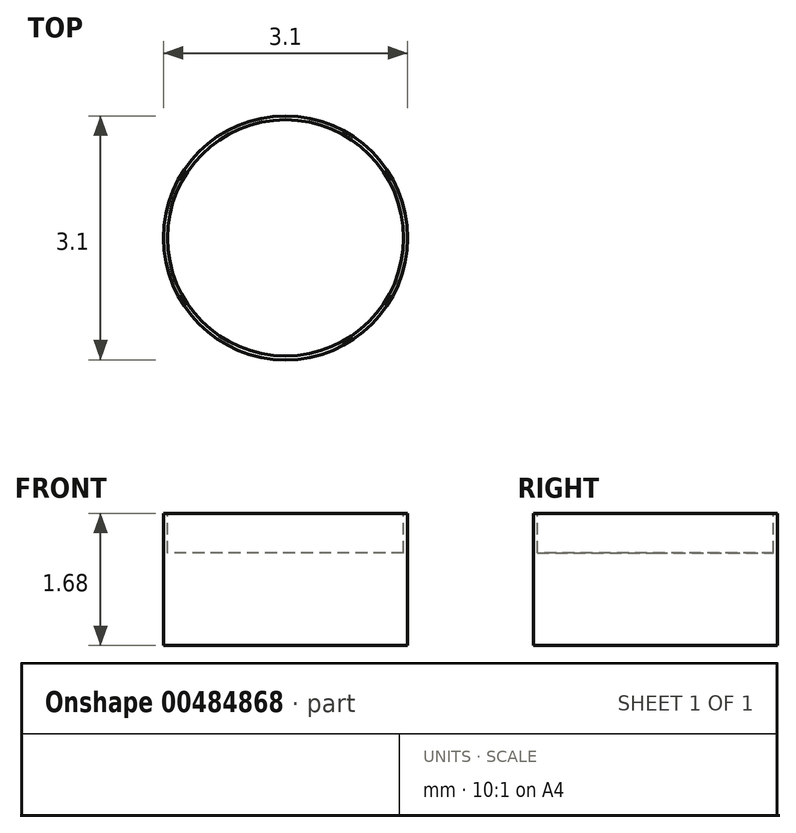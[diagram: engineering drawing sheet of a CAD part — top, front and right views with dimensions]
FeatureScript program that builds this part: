
annotation { "Feature Type Name" : "Feature", "Feature Type Description" : "" }
export const myFeature = defineFeature(function(context is Context, id is Id, definition is map)
    precondition{}
    {
        {
            var Q0;
            Q0=qCreatedBy(makeId("Top.planeOp"),FACE);
            var sketch = newSketch(context, id + "F0", { "sketchPlane" : qUnion([Q0])});
            skCircle(sketch, "E0", {"center": v(0, 0) * mm, "radius": 1.5 * mm});
            skSolve(sketch);
        }
        {
            var Q0;
            Q0=qCreatedBy(makeId("Top.planeOp"),FACE);
            var sketch = newSketch(context, id + "F1", { "sketchPlane" : qUnion([Q0])});
            skCircle(sketch, "E1", {"center": v(0, 0) * mm, "radius": 1.55 * mm});
            skSolve(sketch);
        }
        {
            var Q0;
            Q0=sQuery(id+"F1.wireOp",EDGE,"E1");
            extrude(context, id + "F2", {"bodyType" : ToolBodyType.SURFACE, "surfaceEntities" : qUnion([Q0]), "depth" : 1.68 * mm});
        }
        {
            var Q0;
            Q0=makeQuery(id+"F0.imprint","IMPRINT",FACE,{"disambiguationData":[TD([[makeQuery(id+"F0.imprint","IMPRINT",EDGE,{"derivedFrom":sQuery(id+"F0.wireOp",EDGE,"E0")}),1.0]])]});
            extrude(context, id + "F3", {"entities" : qUnion([Q0]), "depth" : -0.5 * mm});
        }
        {
            var Q0;
            Q0=qCreatedBy(makeId("Top.planeOp"),FACE);
            var sketch = newSketch(context, id + "F4", { "sketchPlane" : qUnion([Q0])});
            skCircle(sketch, "E2", {"center": v(0, 0) * mm, "radius": 1.55 * mm});
            skSolve(sketch);
        }
        {
            var Q0;
            Q0 = qSketchRegion(id + "F4", true);
            extrude(context, id + "F5", {"entities" : qUnion([Q0]), "oppositeDirection" : true, "depth" : 1.68 * mm});
        }
    });
